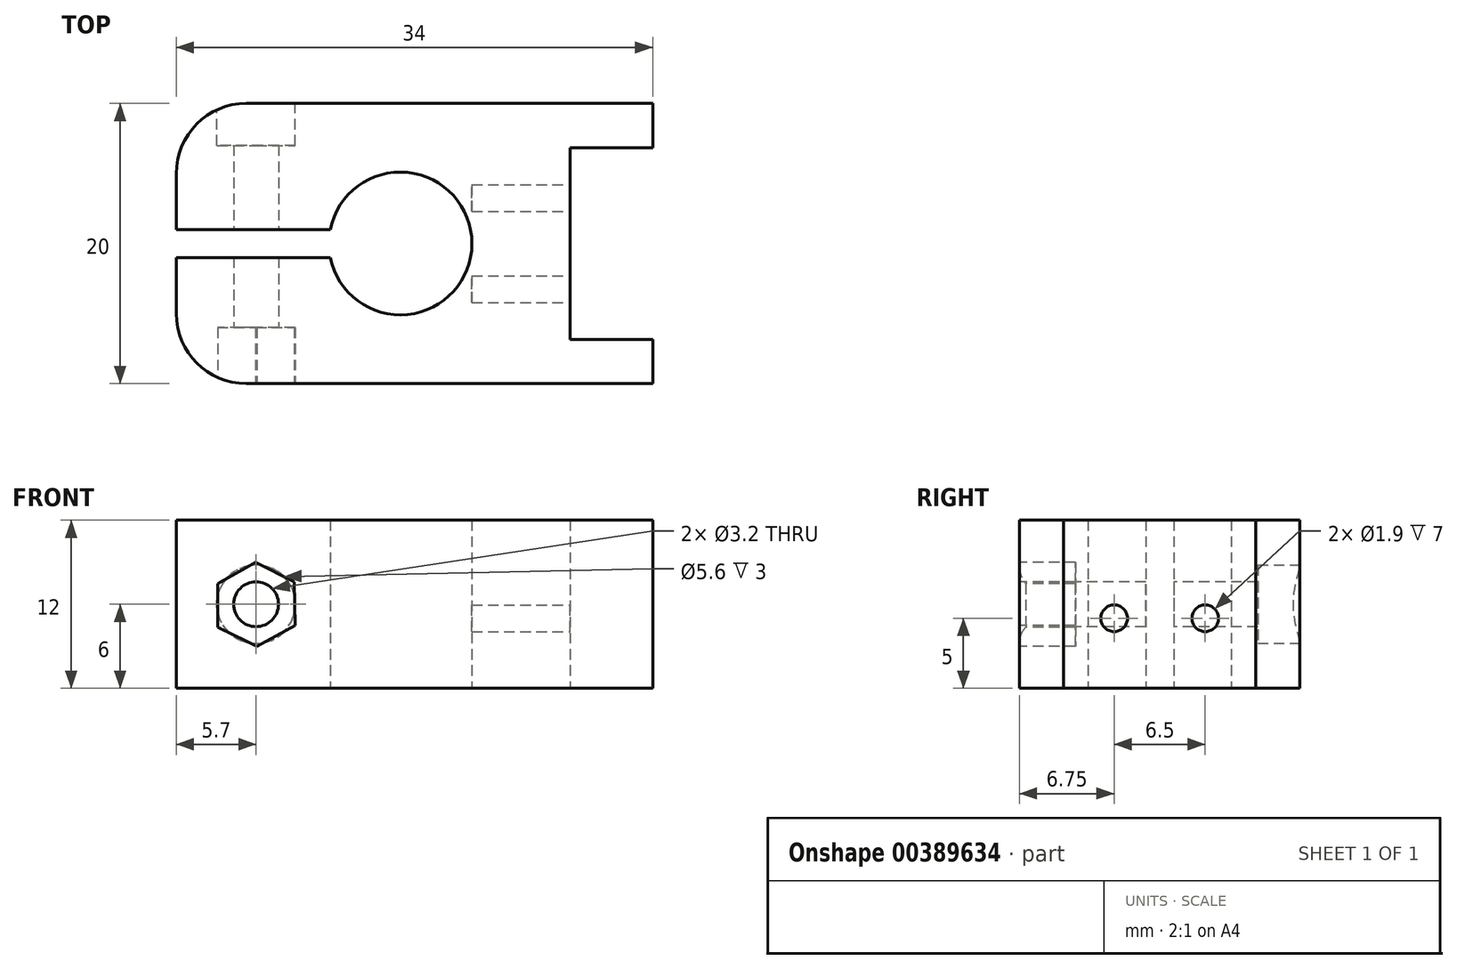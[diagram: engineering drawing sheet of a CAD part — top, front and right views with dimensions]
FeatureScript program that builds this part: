
annotation { "Feature Type Name" : "Feature", "Feature Type Description" : "" }
export const myFeature = defineFeature(function(context is Context, id is Id, definition is map)
    precondition{}
    {
        {
            var Q0;
            Q0=qCreatedBy(makeId("Top.planeOp"),FACE);
            var sketch = newSketch(context, id + "F0", { "sketchPlane" : qUnion([Q0])});
            skLineSegment(sketch, "E0.bottom", {"start": v(-16, 10) * mm, "end": v(18, 10) * mm});
            skLineSegment(sketch, "E0.top", {"start": v(-16, -10) * mm, "end": v(18, -10) * mm});
            skLineSegment(sketch, "E0.left", {"start": v(-16, 10) * mm, "end": v(-16, 1) * mm});
            skLineSegment(sketch, "E0.right", {"start": v(18, 10) * mm, "end": v(18, -10) * mm});
            skArc(sketch, "E1", {"start": v(-5, -1) * mm, "mid": v(5.1, 0) * mm, "end": v(-5, 1) * mm});
            skLineSegment(sketch, "E2.bottom", {"start": v(-16, 0) * mm, "end": v(-4.9, 0) * mm});
            skLineSegment(sketch, "E2.top", {"start": v(-16, 1) * mm, "end": v(-5, 1) * mm});
            skLineSegment(sketch, "E3.MirrorCS", {"start": v(-16, -1) * mm, "end": v(-5, -1) * mm});
            skPoint(sketch, "E4.MirrorCS.end.orphan", {"position": v(-5, -1) * mm});
            skPoint(sketch, "E4.MirrorCS.start.orphan", {"position": v(-4.9, 0) * mm});
            skPoint(sketch, "E5.MirrorCS.end.orphan", {"position": v(-16, -1) * mm});
            skPoint(sketch, "E5.MirrorCS.start.orphan", {"position": v(-16, 0) * mm});
            skLineSegment(sketch, "E6.trimOffspring", {"start": v(-16, -1) * mm, "end": v(-16, -10) * mm});
            skLineSegment(sketch, "E7.bottom", {"start": v(12.1, 6.85) * mm, "end": v(18, 6.85) * mm, "construction": true});
            skLineSegment(sketch, "E7.top", {"start": v(12.1, -6.85) * mm, "end": v(18, -6.85) * mm, "construction": true});
            skLineSegment(sketch, "E7.left", {"start": v(12.1, 6.85) * mm, "end": v(12.1, -6.85) * mm, "construction": true});
            skLineSegment(sketch, "E8.bottom", {"start": v(18, 6.85) * mm, "end": v(18, 6.85) * mm});
            skLineSegment(sketch, "E8.top", {"start": v(14.5, -6.85) * mm, "end": v(18, -6.85) * mm, "construction": true});
            skLineSegment(sketch, "E8.right", {"start": v(18, 6.85) * mm, "end": v(18, -6.85) * mm});
            skLineSegment(sketch, "E9", {"start": v(18, 6.85) * mm, "end": v(18, -6.85) * mm, "construction": true});
            skSolve(sketch);
        }
        {
            var Q0;
            Q0=qSketchRegion(id+"F0",true);
            extrude(context, id + "F1", {"entities" : qUnion([Q0]), "depth" : 12 * mm});
        }
        {
            var Q0;
            Q0=makeQuery(id+"F1.opExtrude","CAP_FACE",FACE,{"disambiguationData":[OSD([sQuery(id+"F0.wireOp",EDGE,"E0.bottom"),sQuery(id+"F0.wireOp",EDGE,"E0.top"),sQuery(id+"F0.wireOp",EDGE,"E0.left"),sQuery(id+"F0.wireOp",EDGE,"E0.right"),sQuery(id+"F0.wireOp",EDGE,"E1"),sQuery(id+"F0.wireOp",EDGE,"E2.top"),sQuery(id+"F0.wireOp",EDGE,"E3.MirrorCS"),sQuery(id+"F0.wireOp",EDGE,"E6.trimOffspring"),sQuery(id+"F0.wireOp",EDGE,"E8.right")])],"isStart":true});
            var sketch = newSketch(context, id + "F2", { "sketchPlane" : qUnion([Q0])});
            skLineSegment(sketch, "E10.0", {"start": v(12.1, -6.85) * mm, "end": v(12.1, 6.85) * mm});
            skLineSegment(sketch, "E11.0", {"start": v(12.1, 6.85) * mm, "end": v(18, 6.85) * mm});
            skLineSegment(sketch, "E12.0", {"start": v(18, 6.85) * mm, "end": v(18, 6.85) * mm});
            skLineSegment(sketch, "E13.0", {"start": v(12.1, -6.85) * mm, "end": v(18, -6.85) * mm});
            skLineSegment(sketch, "E14", {"start": v(18, 6.85) * mm, "end": v(18, -6.85) * mm});
            skSolve(sketch);
        }
        {
            var Q0;
            Q0=qSketchRegion(id+"F2",true);
            extrude(context, id + "F3", {"entities" : qUnion([Q0]), "operationType" : NewBodyOperationType.REMOVE, "endBound" : BoundingType.THROUGH_ALL, "oppositeDirection" : true, "depth" : 10 * mm});
        }
        {
            var Q0;
            Q0=makeQuery(id+"F1.opExtrude","SWEPT_FACE",FACE,{"disambiguationData":[OSD([sQuery(id+"F0.wireOp",EDGE,"E0.top")])]});
            var sketch = newSketch(context, id + "F4", { "sketchPlane" : qUnion([Q0])});
            skCircle(sketch, "E15", {"center": v(-10.3, 6) * mm, "radius": 1.6 * mm});
            skPoint(sketch, "E15.centerSnap0", {"position": v(-16, 6) * mm});
            skSolve(sketch);
        }
        {
            var Q0;
            Q0=qSketchRegion(id+"F4",true);
            extrude(context, id + "F5", {"entities" : qUnion([Q0]), "operationType" : NewBodyOperationType.REMOVE, "endBound" : BoundingType.THROUGH_ALL, "oppositeDirection" : true, "depth" : 25 * mm});
        }
        {
            var Q0;
            Q0=makeQuery(id+"F3.boolean.opBoolean","COPY",FACE,{"derivedFrom":makeQuery(id+"F3.opExtrude","SWEPT_FACE",FACE,{"disambiguationData":[OSD([sQuery(id+"F2.wireOp",EDGE,"E10.0")])]})});
            var sketch = newSketch(context, id + "F6", { "sketchPlane" : qUnion([Q0])});
            skCircle(sketch, "E16", {"center": v(-3.25, 5) * mm, "radius": 0.95 * mm});
            skCircle(sketch, "E17", {"center": v(3.25, 5) * mm, "radius": 0.95 * mm});
            skSolve(sketch);
        }
        {
            var Q0;
            Q0=qSketchRegion(id+"F6",true);
            extrude(context, id + "F7", {"entities" : qUnion([Q0]), "operationType" : NewBodyOperationType.REMOVE, "oppositeDirection" : true, "depth" : 7 * mm});
        }
        {
            var Q0;
            Q0=makeQuery(id+"F1.opExtrude","SWEPT_FACE",FACE,{"disambiguationData":[OSD([sQuery(id+"F0.wireOp",EDGE,"E0.top")])]});
            var sketch = newSketch(context, id + "F8", { "sketchPlane" : qUnion([Q0])});
            skCircle(sketch, "E18.0", {"center": v(-10.3, 6) * mm, "radius": 1.6 * mm, "construction": true});
            skCircle(sketch, "E19", {"center": v(-10.3, 6) * mm, "radius": 2.75 * mm, "construction": true});
            skLineSegment(sketch, "E20", {"start": v(-7.57, 7.6) * mm, "end": v(-7.53, 4.49) * mm});
            skLineSegment(sketch, "E21", {"start": v(-7.53, 4.49) * mm, "end": v(-10.26, 3) * mm});
            skLineSegment(sketch, "E22", {"start": v(-10.26, 3) * mm, "end": v(-13.05, 4.36) * mm});
            skLineSegment(sketch, "E23", {"start": v(-13.05, 4.36) * mm, "end": v(-13.05, 7.47) * mm});
            skLineSegment(sketch, "E24", {"start": v(-13.05, 7.47) * mm, "end": v(-10.34, 9) * mm});
            skLineSegment(sketch, "E25", {"start": v(-10.34, 9) * mm, "end": v(-7.57, 7.6) * mm});
            skSolve(sketch);
        }
        {
            var Q0;
            Q0=qSketchRegion(id+"F8",true);
            extrude(context, id + "F9", {"entities" : qUnion([Q0]), "operationType" : NewBodyOperationType.REMOVE, "oppositeDirection" : true, "depth" : 4 * mm});
        }
        {
            var Q0;
            Q0=makeQuery(id+"F1.opExtrude","SWEPT_FACE",FACE,{"disambiguationData":[OSD([sQuery(id+"F0.wireOp",EDGE,"E0.bottom")])]});
            var sketch = newSketch(context, id + "F10", { "sketchPlane" : qUnion([Q0])});
            skPoint(sketch, "E26", {"position": v(10.3, 6) * mm});
            skCircle(sketch, "E27", {"center": v(10.3, 6) * mm, "radius": 2.8 * mm});
            skSolve(sketch);
        }
        {
            var Q0;
            Q0=qSketchRegion(id+"F10",true);
            extrude(context, id + "F11", {"entities" : qUnion([Q0]), "operationType" : NewBodyOperationType.REMOVE, "oppositeDirection" : true, "depth" : 3 * mm});
        }
        {
            var Q0;
            Q0=makeQuery(id+"F1.opExtrude","SWEPT_EDGE",EDGE,{"disambiguationData":[OSD([sQuery(id+"F0.wireOp",EDGE,"E0.top"),sQuery(id+"F0.wireOp",EDGE,"E6.trimOffspring")])]});
            var Q1;
            Q1=makeQuery(id+"F1.opExtrude","SWEPT_EDGE",EDGE,{"disambiguationData":[OSD([sQuery(id+"F0.wireOp",EDGE,"E0.bottom"),sQuery(id+"F0.wireOp",EDGE,"E0.left")])]});
            fillet(context, id + "F12", {"entities" : qUnion([Q0, Q1]), "radius" : 5 * mm, "tangentPropagation" : true, "allowEdgeOverflow" : false});
        }
    });
